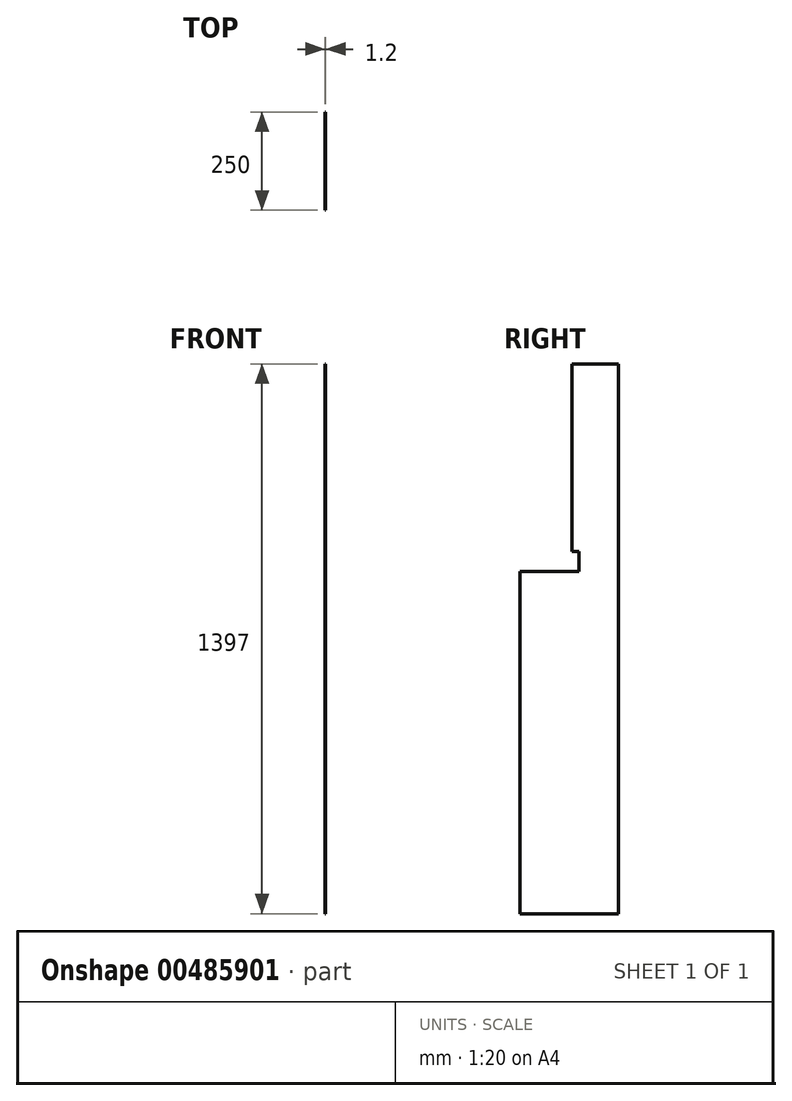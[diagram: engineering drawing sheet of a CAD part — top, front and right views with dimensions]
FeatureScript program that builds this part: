
annotation { "Feature Type Name" : "Feature", "Feature Type Description" : "" }
export const myFeature = defineFeature(function(context is Context, id is Id, definition is map)
    precondition{}
    {
        {
            var Q0;
            Q0=qCreatedBy(makeId("Right.planeOp"),FACE);
            var sketch = newSketch(context, id + "F0", { "sketchPlane" : qUnion([Q0])});
            skLineSegment(sketch, "E0", {"start": v(0, 0) * mm, "end": v(0, 1397) * mm});
            skLineSegment(sketch, "E1", {"start": v(0, 1397) * mm, "end": v(-118, 1397) * mm});
            skLineSegment(sketch, "E2", {"start": v(-118, 1397) * mm, "end": v(-118, 920) * mm});
            skLineSegment(sketch, "E3", {"start": v(-118, 920) * mm, "end": v(-100, 920) * mm});
            skLineSegment(sketch, "E4", {"start": v(-100, 920) * mm, "end": v(-100, 870) * mm});
            skLineSegment(sketch, "E5", {"start": v(-100, 870) * mm, "end": v(-250, 870) * mm});
            skLineSegment(sketch, "E6", {"start": v(-250, 870) * mm, "end": v(-250, 0) * mm});
            skLineSegment(sketch, "E7", {"start": v(-250, 0) * mm, "end": v(0, 0) * mm});
            skSolve(sketch);
        }
        {
            var Q0;
            Q0=qSketchRegion(id+"F0",true);
            extrude(context, id + "F1", {"entities" : qUnion([Q0]), "depth" : 1.2 * mm});
        }
    });
